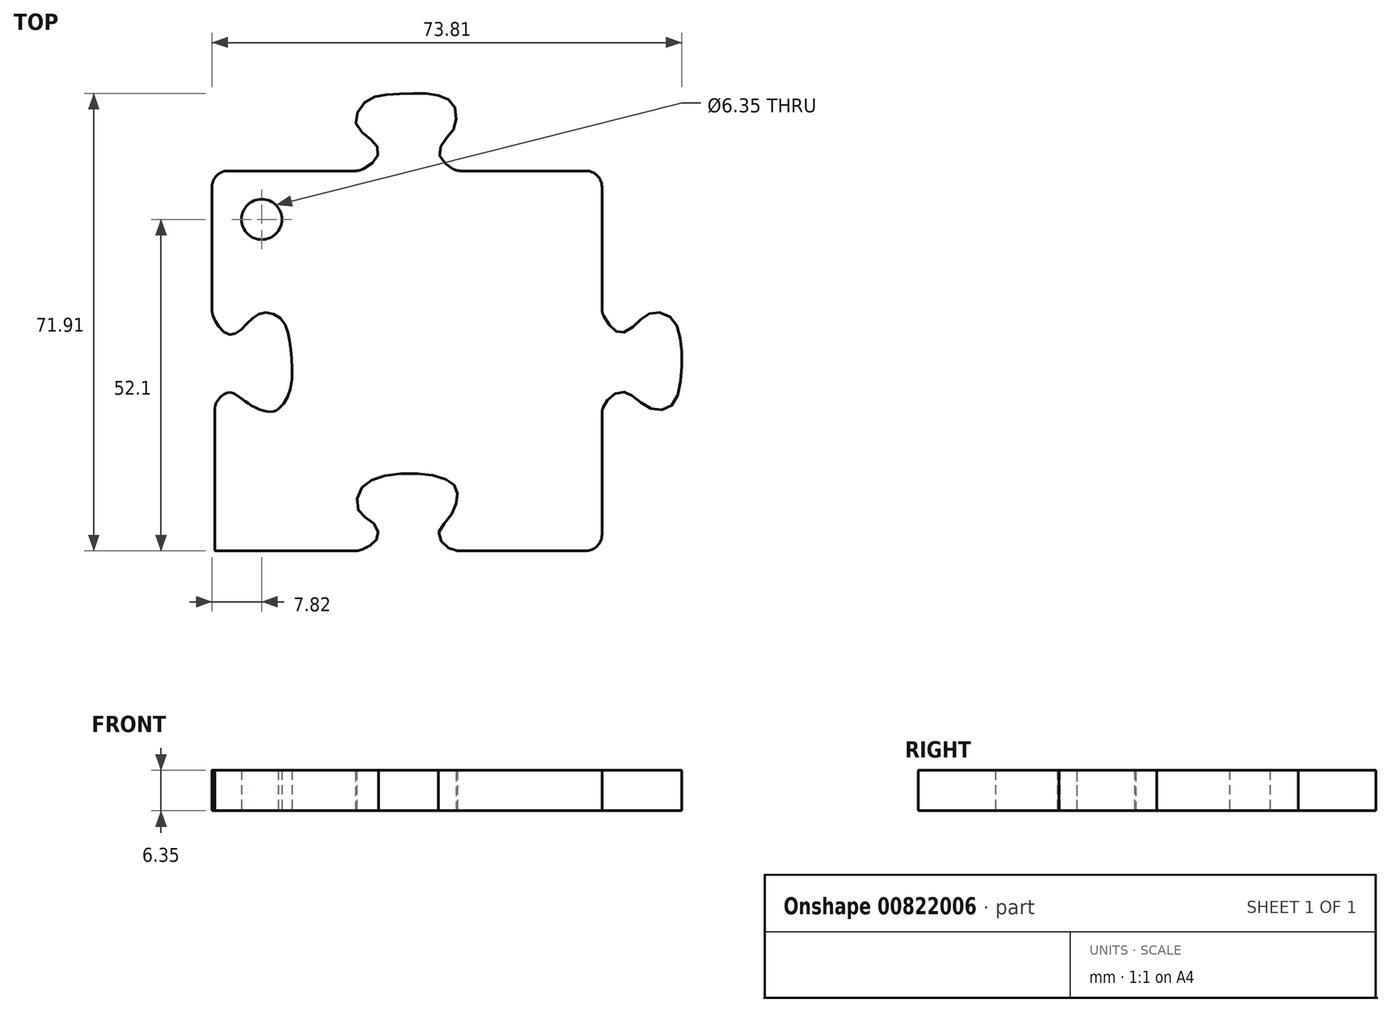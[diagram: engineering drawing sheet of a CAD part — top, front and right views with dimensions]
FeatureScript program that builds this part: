
annotation { "Feature Type Name" : "Feature", "Feature Type Description" : "" }
export const myFeature = defineFeature(function(context is Context, id is Id, definition is map)
    precondition{}
    {
        {
            var Q0;
            Q0=qCreatedBy(makeId("Top.planeOp"),FACE);
            var sketch = newSketch(context, id + "F0", { "sketchPlane" : qUnion([Q0])});
            skLineSegment(sketch, "E0.bottom", {"start": v(25.4, 25.4) * mm, "end": v(-25.4, 25.4) * mm, "construction": true});
            skLineSegment(sketch, "E0.top", {"start": v(25.4, -25.4) * mm, "end": v(-25.4, -25.4) * mm, "construction": true});
            skLineSegment(sketch, "E0.left", {"start": v(25.4, 25.4) * mm, "end": v(25.4, -25.4) * mm, "construction": true});
            skLineSegment(sketch, "E0.right", {"start": v(-25.4, 25.4) * mm, "end": v(-25.4, -25.4) * mm, "construction": true});
            skPoint(sketch, "E0.middle", {"position": v(0, 0) * mm});
            skLineSegment(sketch, "E1", {"start": v(-34.74, 25.07) * mm, "end": v(-14.72, 25.07) * mm});
            skLineSegment(sketch, "E2", {"start": v(1.8, 25.07) * mm, "end": v(21.44, 25.07) * mm});
            skLineSegment(sketch, "E3", {"start": v(23.98, 22.53) * mm, "end": v(23.98, 3.43) * mm});
            skLineSegment(sketch, "E4", {"start": v(23.98, -13.05) * mm, "end": v(23.98, -32.1) * mm});
            skLineSegment(sketch, "E5", {"start": v(21.44, -34.65) * mm, "end": v(1.58, -34.65) * mm});
            skLineSegment(sketch, "E6", {"start": v(-14.73, -34.65) * mm, "end": v(-36.83, -34.65) * mm});
            skLineSegment(sketch, "E7", {"start": v(-36.83, -34.65) * mm, "end": v(-36.83, -12.61) * mm});
            skLineSegment(sketch, "E8", {"start": v(-37.28, 22.53) * mm, "end": v(-37.28, 3.23) * mm});
            skFitSpline(sketch, "E9", {"points": [v(-37.28, 2.8) * mm, v(-36.64, 1.29) * mm, v(-35.04, -0.48) * mm, v(-33.35, -0.4) * mm, v(-31.2, 1.66) * mm, v(-28.94, 2.8) * mm, v(-26.31, 1.7) * mm, v(-25.12, -1.43) * mm, v(-24.7, -5.26) * mm, v(-25.16, -9.99) * mm, v(-26.89, -12.38) * mm], "startDerivative": vector(6.42, -18.91) * mm, "endDerivative": vector(-20.24, -18.94) * mm});
            skFitSpline(sketch, "E10", {"points": [v(-26.89, -12.38) * mm, v(-28.16, -12.79) * mm, v(-30.88, -11.92) * mm, v(-33.06, -10.4) * mm, v(-34.79, -9.78) * mm, v(-36.64, -11.43) * mm, v(-36.83, -12.61) * mm], "startDerivative": vector(-7.22, -6.07) * mm, "endDerivative": vector(0.38, -8.5) * mm});
            skFitSpline(sketch, "E11", {"points": [v(-14.1, 25.07) * mm, v(-11.66, 26.72) * mm, v(-11.17, 28.59) * mm, v(-12.9, 30.5) * mm, v(-14.68, 32.77) * mm, v(-13.17, 35.92) * mm, v(-9.97, 37.03) * mm, v(-5.62, 37.26) * mm, v(-1.48, 36.9) * mm, v(0.74, 35.39) * mm, v(0.87, 32.06) * mm, v(-0.64, 29.97) * mm, v(-1.57, 27.66) * mm, v(0, 25.74) * mm, v(1.21, 25.07) * mm], "startDerivative": vector(38.72, 19.86) * mm, "endDerivative": vector(22.38, -10.51) * mm});
            skArc(sketch, "E12.filletArc", {"start": v(-14.72, 25.07) * mm, "mid": v(-14.1, 25.15) * mm, "end": v(-13.53, 25.37) * mm});
            skArc(sketch, "E13.filletArc", {"start": v(0.58, 25.38) * mm, "mid": v(1.17, 25.15) * mm, "end": v(1.8, 25.07) * mm});
            skArc(sketch, "E14.filletArc", {"start": v(-37.28, 3.23) * mm, "mid": v(-37.24, 2.8) * mm, "end": v(-37.12, 2.36) * mm});
            skPoint(sketch, "E15.visualSharp", {"position": v(-37.28, 25.07) * mm});
            skArc(sketch, "E15.filletArc", {"start": v(-34.74, 25.07) * mm, "mid": v(-36.53, 24.33) * mm, "end": v(-37.28, 22.53) * mm});
            skPoint(sketch, "E16.visualSharp", {"position": v(23.98, 25.07) * mm});
            skArc(sketch, "E16.filletArc", {"start": v(23.98, 22.53) * mm, "mid": v(23.23, 24.33) * mm, "end": v(21.44, 25.07) * mm});
            skFitSpline(sketch, "E17", {"points": [v(23.98, 2.8) * mm, v(25.52, 0.39) * mm, v(27.2, -0.36) * mm, v(29.53, 1.22) * mm, v(31.86, 2.8) * mm, v(34.85, 1.93) * mm, v(36.35, -1.55) * mm, v(36.4, -7.14) * mm, v(35.03, -11.72) * mm, v(32.12, -12.42) * mm, v(29.09, -10.58) * mm, v(27.2, -9.65) * mm, v(24.9, -10.84) * mm, v(23.98, -12.6) * mm], "startDerivative": vector(18.91, -35.94) * mm, "endDerivative": vector(-10.25, -29.43) * mm});
            skArc(sketch, "E18.filletArc", {"start": v(23.98, 3.43) * mm, "mid": v(24.05, 2.8) * mm, "end": v(24.28, 2.22) * mm});
            skArc(sketch, "E19.filletArc", {"start": v(24.14, -12.14) * mm, "mid": v(24.02, -12.59) * mm, "end": v(23.98, -13.05) * mm});
            skPoint(sketch, "E20.visualSharp", {"position": v(23.98, -34.65) * mm});
            skArc(sketch, "E20.filletArc", {"start": v(21.44, -34.65) * mm, "mid": v(23.23, -33.9) * mm, "end": v(23.98, -32.1) * mm});
            skFitSpline(sketch, "E21", {"points": [v(-14.2, -34.65) * mm, v(-12.28, -33.67) * mm, v(-11.13, -32.16) * mm, v(-12.02, -30.22) * mm, v(-14.2, -28.43) * mm, v(-13.9, -24.94) * mm, v(-9.94, -22.83) * mm, v(-3.05, -22.72) * mm, v(0.61, -24.19) * mm, v(1.26, -26.2) * mm, v(0, -29.43) * mm, v(-1.68, -31.98) * mm, v(-0.32, -34.06) * mm, v(1.35, -34.65) * mm], "startDerivative": vector(30.63, 12.93) * mm, "endDerivative": vector(27.87, -5.12) * mm});
            skArc(sketch, "E22.filletArc", {"start": v(1.1, -34.6) * mm, "mid": v(1.34, -34.64) * mm, "end": v(1.58, -34.65) * mm});
            skArc(sketch, "E23.filletArc", {"start": v(-14.73, -34.65) * mm, "mid": v(-14.2, -34.6) * mm, "end": v(-13.7, -34.43) * mm});
            skLineSegment(sketch, "E24", {"start": v(-37.28, 25.07) * mm, "end": v(23.98, -34.65) * mm, "construction": true});
            skCircle(sketch, "E25", {"center": v(-29.46, 17.45) * mm, "radius": 3.18 * mm});
            skSolve(sketch);
        }
        {
            var Q0;
            Q0=qSketchRegion(id+"F0",true);
            extrude(context, id + "F1", {"entities" : qUnion([Q0]), "depth" : 6.35 * mm});
        }
    });
